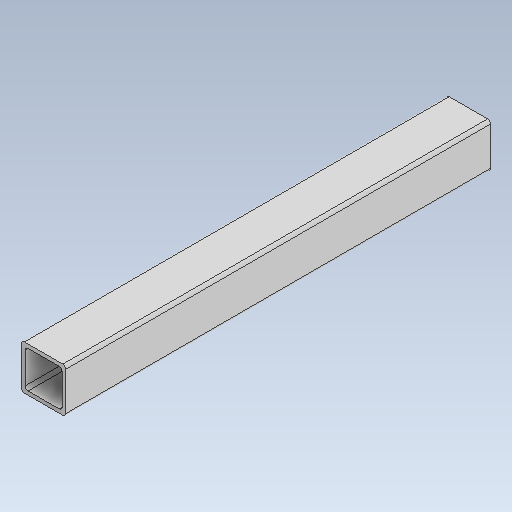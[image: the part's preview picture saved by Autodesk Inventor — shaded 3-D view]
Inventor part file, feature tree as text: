
AUTODESK INVENTOR PART (.ipt)
format: ipt  version: 2021 (Build 250183000, 183)  size: 134,144 bytes
history: native  units: mm
features: extrude x2, fillet x2, sketch x2
ambient origin geometry x8: Origin, YZ Plane, XZ Plane, XY Plane, X Axis, Y Axis, Z Axis, Center Point
bodies: Solid1 (feature_tree)
feature tree (6):
  extrude  "Extrusion1"  Depth=30.0mm
  fillet  "Fillet1"  Radius=30.0mm
  extrude  "Extrusion2"  Depth=30.0mm TaperAngle=0.0deg
  fillet  "Fillet2"  Radius=2.0mm
  sketch  "Sketch1"  dims[d0=287.5mm d1=143.75mm d2=30.0mm]
  sketch  "Sketch2"  dims[d3=15.0mm d4=30.0mm d5=0.0mm d6=2.0mm d7=2.5mm d8=2.5mm d9=2.5mm d10=2.5mm d11=300.0mm d12=0.0mm d13=2.0mm]
